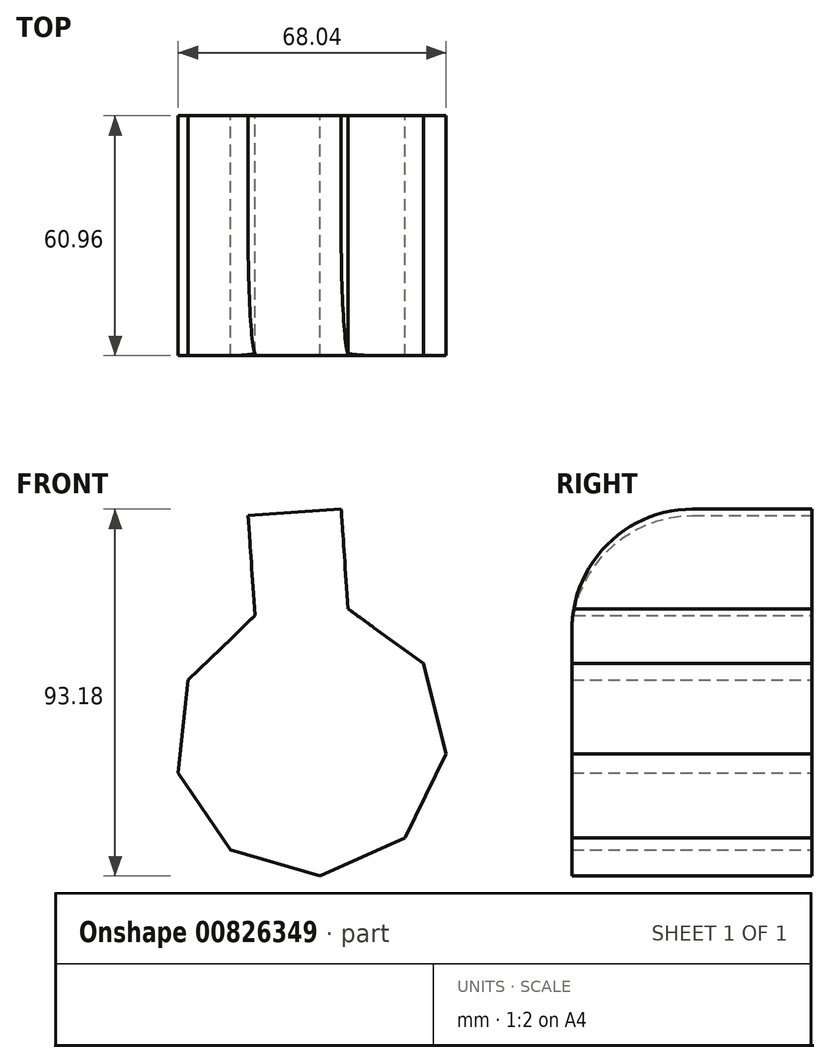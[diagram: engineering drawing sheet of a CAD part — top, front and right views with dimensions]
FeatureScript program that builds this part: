
annotation { "Feature Type Name" : "Feature", "Feature Type Description" : "" }
export const myFeature = defineFeature(function(context is Context, id is Id, definition is map)
    precondition{}
    {
        {
            var Q0;
            Q0=qCreatedBy(makeId("Front.planeOp"),FACE);
            var sketch = newSketch(context, id + "F0", { "sketchPlane" : qUnion([Q0])});
            skCircle(sketch, "E0.cCircle", {"center": v(0, 0) * mm, "radius": 32.54 * mm, "construction": true});
            skLineSegment(sketch, "E0.0", {"start": v(34.44, -3.63) * mm, "end": v(24.05, -24.92) * mm});
            skLineSegment(sketch, "E0.1", {"start": v(24.05, -24.92) * mm, "end": v(2.4, -34.55) * mm});
            skLineSegment(sketch, "E0.2", {"start": v(2.4, -34.55) * mm, "end": v(-20.36, -28.01) * mm});
            skLineSegment(sketch, "E0.3", {"start": v(-20.36, -28.01) * mm, "end": v(-33.6, -8.37) * mm});
            skLineSegment(sketch, "E0.4", {"start": v(-33.6, -8.37) * mm, "end": v(-31.12, 15.19) * mm});
            skLineSegment(sketch, "E0.5", {"start": v(-31.12, 15.19) * mm, "end": v(-14.08, 31.64) * mm});
            skLineSegment(sketch, "E0.6", {"start": v(-14.08, 31.64) * mm, "end": v(9.55, 33.29) * mm});
            skLineSegment(sketch, "E0.7", {"start": v(9.55, 33.29) * mm, "end": v(28.71, 19.36) * mm});
            skLineSegment(sketch, "E0.8", {"start": v(28.71, 19.36) * mm, "end": v(34.44, -3.63) * mm});
            skPoint(sketch, "E0.0.midPoint", {"position": v(29.25, -14.27) * mm});
            skSolve(sketch);
        }
        {
            var Q0;
            Q0=makeQuery(id+"F0.imprint","IMPRINT",FACE,{"disambiguationData":[TD([[makeQuery(id+"F0.imprint","IMPRINT",EDGE,{"derivedFrom":sQuery(id+"F0.wireOp",EDGE,"E0.0")}),-1.0]])]});
            extrude(context, id + "F1", {"entities" : qUnion([Q0]), "depth" : 60.96 * mm, "offsetDistance" : 25.4 * mm});
        }
        {
            var Q0;
            Q0=makeQuery(id+"F1.opExtrude","SWEPT_FACE",FACE,{"disambiguationData":[OSD([sQuery(id+"F0.wireOp",EDGE,"E0.6")])]});
            extrude(context, id + "F2", {"entities" : qUnion([Q0]), "operationType" : NewBodyOperationType.ADD, "depth" : 25.4 * mm, "offsetDistance" : 25.4 * mm});
        }
        {
            var Q0;
            {var subQ0=sQuery(id+"F0.wireOp",EDGE,"E0.6");Q0=makeQuery(id+"F2.opExtrude","CAP_EDGE",EDGE,{"disambiguationData":[OSD([subQ0]),TDD([makeQuery(id+"F1.opExtrude","CAP_EDGE",EDGE,{"disambiguationData":[OSD([subQ0])],"isStart":false})])],"isStart":false});}
            fillet(context, id + "F3", {"entities" : qUnion([Q0]), "radius" : 30.66 * mm, "tangentPropagation" : true, "allowEdgeOverflow" : false});
        }
    });
